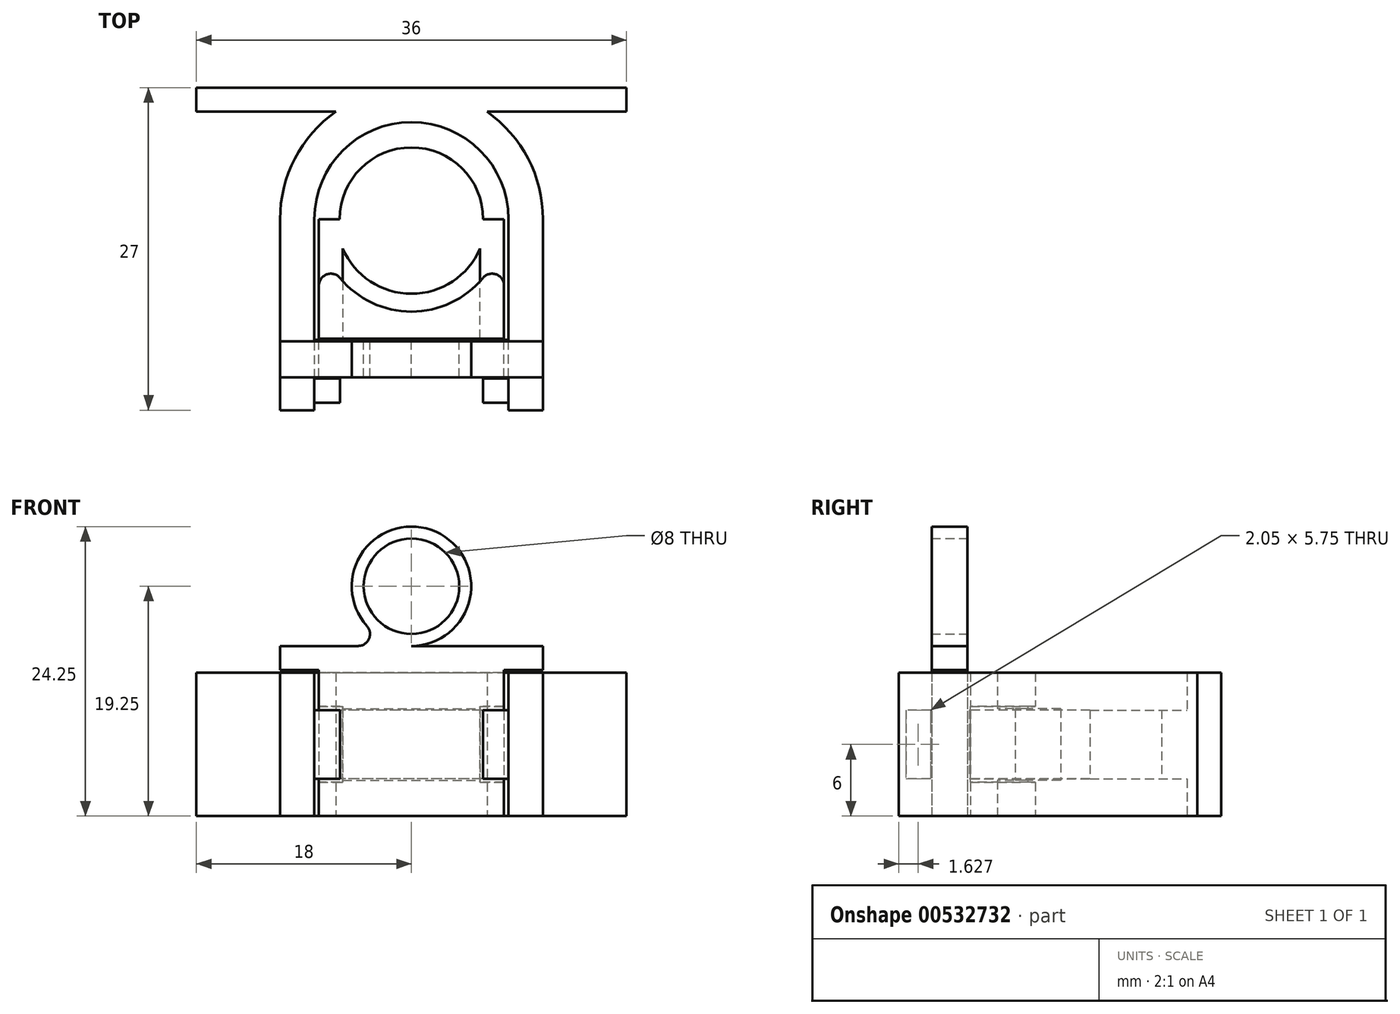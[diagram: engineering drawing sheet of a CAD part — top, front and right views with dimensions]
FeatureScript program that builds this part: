
annotation { "Feature Type Name" : "Feature", "Feature Type Description" : "" }
export const myFeature = defineFeature(function(context is Context, id is Id, definition is map)
    precondition{}
    {
        {
            var Q0;
            Q0=qCreatedBy(makeId("Top.planeOp"),FACE);
            var sketch = newSketch(context, id + "F0", { "sketchPlane" : qUnion([Q0])});
            skLineSegment(sketch, "E0", {"start": v(16.68, 0) * mm, "end": v(-18.88, 0) * mm, "construction": true});
            skLineSegment(sketch, "E1", {"start": v(-8.12, 0) * mm, "end": v(-8.12, -16) * mm});
            skLineSegment(sketch, "E2", {"start": v(-8.12, -16) * mm, "end": v(-11, -16) * mm});
            skLineSegment(sketch, "E3", {"start": v(-11, -16) * mm, "end": v(-11, 0) * mm});
            skLineSegment(sketch, "E4", {"start": v(11, 0) * mm, "end": v(11, -16) * mm});
            skLineSegment(sketch, "E5", {"start": v(11, -16) * mm, "end": v(8.12, -16) * mm});
            skLineSegment(sketch, "E6", {"start": v(8.12, -16) * mm, "end": v(8.12, 0) * mm});
            skArc(sketch, "E7", {"start": v(-8.12, 0) * mm, "mid": v(0, -8.12) * mm, "end": v(8.12, 0) * mm, "construction": true});
            skArc(sketch, "E8", {"start": v(8.12, 0) * mm, "mid": v(0, 8.12) * mm, "end": v(-8.12, 0) * mm});
            skArc(sketch, "E9", {"start": v(11, 0) * mm, "mid": v(0, 11) * mm, "end": v(-11, 0) * mm});
            skArc(sketch, "E10", {"start": v(-11, 0) * mm, "mid": v(0, -11) * mm, "end": v(11, 0) * mm, "construction": true});
            skArc(sketch, "E11", {"start": v(-5.99, -0.4) * mm, "mid": v(0, -6) * mm, "end": v(5.99, -0.4) * mm, "construction": true});
            skArc(sketch, "E12", {"start": v(5.99, -0.4) * mm, "mid": v(0, 6) * mm, "end": v(-5.99, -0.4) * mm});
            skLineSegment(sketch, "E13", {"start": v(0, 11) * mm, "end": v(-18, 11) * mm});
            skLineSegment(sketch, "E14", {"start": v(-18, 11) * mm, "end": v(-18, 9) * mm});
            skLineSegment(sketch, "E15", {"start": v(-18, 9) * mm, "end": v(-6.32, 9) * mm});
            skLineSegment(sketch, "E16", {"start": v(0, -19.46) * mm, "end": v(0, 22.13) * mm, "construction": true});
            skLineSegment(sketch, "E17.MirrorCS", {"start": v(0, 11) * mm, "end": v(18, 11) * mm});
            skLineSegment(sketch, "E18.MirrorCS", {"start": v(18, 9) * mm, "end": v(6.32, 9) * mm});
            skLineSegment(sketch, "E19.MirrorCS", {"start": v(18, 11) * mm, "end": v(18, 9) * mm});
            skLineSegment(sketch, "E20", {"start": v(-5.99, -0.4) * mm, "end": v(-5.99, -15.4) * mm});
            skLineSegment(sketch, "E21", {"start": v(-5.99, -15.4) * mm, "end": v(-8.12, -15.4) * mm});
            skLineSegment(sketch, "E22", {"start": v(5.99, -0.4) * mm, "end": v(5.99, -15.4) * mm});
            skLineSegment(sketch, "E23", {"start": v(5.99, -15.4) * mm, "end": v(8.12, -15.4) * mm});
            skLineSegment(sketch, "E24", {"start": v(-5.99, -10.1) * mm, "end": v(-8.12, -10.1) * mm});
            skLineSegment(sketch, "E25", {"start": v(-5.99, -13.35) * mm, "end": v(-8.12, -13.35) * mm});
            skLineSegment(sketch, "E26.MirrorCS", {"start": v(5.99, -10.1) * mm, "end": v(8.12, -10.1) * mm});
            skLineSegment(sketch, "E27.MirrorCS", {"start": v(5.99, -13.35) * mm, "end": v(8.12, -13.35) * mm});
            skSolve(sketch);
        }
        {
            var Q0;
            {var subQ0=sQuery(id+"F0.wireOp",EDGE,"E13");Q0=makeQuery(id+"F0.imprint","IMPRINT",FACE,{"disambiguationData":[TD([[makeQuery(id+"F0.imprint","IMPRINT",EDGE,{"derivedFrom":subQ0}),1.0]])]});}
            var Q1;
            {var subQ0=sQuery(id+"F0.wireOp",EDGE,"E17.MirrorCS");Q1=makeQuery(id+"F0.imprint","IMPRINT",FACE,{"disambiguationData":[TD([[makeQuery(id+"F0.imprint","IMPRINT",EDGE,{"derivedFrom":subQ0}),-1.0]])]});}
            var Q2;
            {var subQ9=sQuery(id+"F0.wireOp",EDGE,"E2");Q2=makeQuery(id+"F0.imprint","IMPRINT",FACE,{"disambiguationData":[TD([[makeQuery(id+"F0.imprint","IMPRINT",EDGE,{"derivedFrom":subQ9}),-1.0]])]});}
            extrude(context, id + "F1", {"entities" : qUnion([Q0, Q1, Q2]), "endBound" : BoundingType.SYMMETRIC, "depth" : 12 * mm, "offsetDistance" : 25 * mm});
        }
        {
            var Q0;
            {var subQ0=sQuery(id+"F0.wireOp",EDGE,"E8");Q0=makeQuery(id+"F0.imprint","IMPRINT",FACE,{"disambiguationData":[TD([[makeQuery(id+"F0.imprint","IMPRINT",EDGE,{"derivedFrom":subQ0}),1.0]])]});}
            var Q1;
            {var subQ0=sQuery(id+"F0.wireOp",EDGE,"E21");Q1=makeQuery(id+"F0.imprint","IMPRINT",FACE,{"disambiguationData":[TD([[makeQuery(id+"F0.imprint","IMPRINT",EDGE,{"derivedFrom":subQ0}),-1.0]])]});}
            var Q2;
            {var subQ0=sQuery(id+"F0.wireOp",EDGE,"E23");Q2=makeQuery(id+"F0.imprint","IMPRINT",FACE,{"disambiguationData":[TD([[makeQuery(id+"F0.imprint","IMPRINT",EDGE,{"derivedFrom":subQ0}),1.0]])]});}
            var Q3;
            Q3=sQuery(id+"F0.wireOp",EDGE,"E8");
            extrude(context, id + "F2", {"entities" : qUnion([Q0, Q1, Q2]), "operationType" : NewBodyOperationType.ADD, "surfaceEntities" : qUnion([Q3]), "endBound" : BoundingType.SYMMETRIC, "depth" : 5.75 * mm, "offsetDistance" : 25 * mm});
        }
        {
            var Q0;
            Q0=qCreatedBy(makeId("Top.planeOp"),FACE);
            var sketch = newSketch(context, id + "F3", { "sketchPlane" : qUnion([Q0])});
            skLineSegment(sketch, "E28", {"start": v(0, 21.73) * mm, "end": v(0, -21.78) * mm, "construction": true});
            skLineSegment(sketch, "E29", {"start": v(-21.07, 0) * mm, "end": v(6.25, 0) * mm, "construction": true});
            skLineSegment(sketch, "E30", {"start": v(-5.75, -2.45) * mm, "end": v(-5.75, -10) * mm});
            skLineSegment(sketch, "E31", {"start": v(5.75, -10) * mm, "end": v(5.75, -2.45) * mm});
            skLineSegment(sketch, "E32", {"start": v(-7.75, 0) * mm, "end": v(-7.75, -10) * mm});
            skLineSegment(sketch, "E33", {"start": v(-7.75, -10) * mm, "end": v(7.75, -10) * mm});
            skLineSegment(sketch, "E34", {"start": v(7.75, -10) * mm, "end": v(7.75, 0) * mm});
            skArc(sketch, "E35", {"start": v(-7.75, 0) * mm, "mid": v(0, -7.75) * mm, "end": v(7.75, 0) * mm});
            skArc(sketch, "E36", {"start": v(7.75, 0) * mm, "mid": v(0, 7.75) * mm, "end": v(-7.75, 0) * mm, "construction": true});
            skLineSegment(sketch, "E37", {"start": v(6.25, 0) * mm, "end": v(23.4, 0) * mm, "construction": true});
            skArc(sketch, "E38", {"start": v(-5.75, -2.45) * mm, "mid": v(0, -6.25) * mm, "end": v(5.75, -2.45) * mm});
            skArc(sketch, "E39", {"start": v(5.75, -2.45) * mm, "mid": v(0, 6.25) * mm, "end": v(-5.75, -2.45) * mm, "construction": true});
            skLineSegment(sketch, "E40", {"start": v(5.75, -2.45) * mm, "end": v(5.75, 0) * mm});
            skLineSegment(sketch, "E41", {"start": v(5.75, 0) * mm, "end": v(7.75, 0) * mm});
            skLineSegment(sketch, "E42", {"start": v(-5.75, -2.45) * mm, "end": v(-5.75, 0) * mm});
            skLineSegment(sketch, "E43", {"start": v(-5.75, 0) * mm, "end": v(-7.75, 0) * mm});
            skSolve(sketch);
        }
        {
            var Q0;
            {var subQ5=sQuery(id+"F3.wireOp",EDGE,"E32");Q0=makeQuery(id+"F3.imprint","IMPRINT",FACE,{"disambiguationData":[TD([[makeQuery(id+"F3.imprint","IMPRINT",EDGE,{"derivedFrom":subQ5}),1.0]])]});}
            var Q1;
            {var subQ1=sQuery(id+"F3.wireOp",EDGE,"wfdL85CV-VBdl-9YlV-2M5o-2CQI3bBZQMcm");var subQ5=sQuery(id+"F3.wireOp",EDGE,"E30");var subQ6=makeQuery(id+"F3.imprint","INTERSECT",VERTEX,{"derivedFrom":[subQ1,subQ5]});Q1=makeQuery(id+"F3.imprint","IMPRINT",FACE,{"disambiguationData":[TD([[makeQuery(id+"F3.imprint","IMPRINT",EDGE,{"disambiguationData":[TD([[subQ6,1.0]])],"derivedFrom":subQ1}),-1.0]])]});}
            var Q2;
            {var subQ0=sQuery(id+"F3.wireOp",EDGE,"E30");var subQ1=sQuery(id+"F3.wireOp",EDGE,"wfdL85CV-VBdl-9YlV-2M5o-2CQI3bBZQMcm");var subQ2=makeQuery(id+"F3.imprint","INTERSECT",VERTEX,{"derivedFrom":[subQ1,subQ0]});Q2=makeQuery(id+"F3.imprint","IMPRINT",FACE,{"disambiguationData":[TD([[makeQuery(id+"F3.imprint","IMPRINT",EDGE,{"disambiguationData":[TD([[subQ2,-1.0]])],"derivedFrom":subQ1}),-1.0]])]});}
            var Q3;
            {var subQ0=sQuery(id+"F3.wireOp",EDGE,"E33");var subQ1=sQuery(id+"F3.wireOp",EDGE,"E30");var subQ2=makeQuery(id+"F3.imprint","INTERSECT",VERTEX,{"derivedFrom":[subQ1,subQ0]});Q3=makeQuery(id+"F3.imprint","IMPRINT",FACE,{"disambiguationData":[TD([[makeQuery(id+"F3.imprint","IMPRINT",EDGE,{"disambiguationData":[TD([[subQ2,1.0]])],"derivedFrom":subQ1}),1.0]])]});}
            var Q4;
            {var subQ5=sQuery(id+"F3.wireOp",EDGE,"E34");Q4=makeQuery(id+"F3.imprint","IMPRINT",FACE,{"disambiguationData":[TD([[makeQuery(id+"F3.imprint","IMPRINT",EDGE,{"derivedFrom":subQ5}),1.0]])]});}
            var Q5;
            {var subQ0=sQuery(id+"F3.wireOp",EDGE,"wfdL85CV-VBdl-9YlV-2M5o-2CQI3bBZQMcm");var subQ1=makeQuery(id+"F3.imprint","INTERSECT",VERTEX,{"derivedFrom":[subQ0,sQuery(id+"F3.wireOp",EDGE,"E30")]});Q5=makeQuery(id+"F3.imprint","IMPRINT",FACE,{"disambiguationData":[TD([[makeQuery(id+"F3.imprint","IMPRINT",EDGE,{"disambiguationData":[TD([[subQ1,-1.0]])],"derivedFrom":subQ0}),1.0]])]});}
            extrude(context, id + "F4", {"entities" : qUnion([Q0, Q1, Q2, Q3, Q4, Q5]), "endBound" : BoundingType.SYMMETRIC, "depth" : 12 * mm, "offsetDistance" : 25 * mm});
        }
        {
            var Q0;
            {var subQ0=sQuery(id+"F3.wireOp",EDGE,"E38");Q0=makeQuery(id+"F3.imprint","IMPRINT",FACE,{"disambiguationData":[TD([[makeQuery(id+"F3.imprint","IMPRINT",EDGE,{"derivedFrom":subQ0}),-1.0]])]});}
            extrude(context, id + "F5", {"entities" : qUnion([Q0]), "operationType" : NewBodyOperationType.ADD, "endBound" : BoundingType.SYMMETRIC, "depth" : 6 * mm, "offsetDistance" : 25 * mm});
        }
        {
            var Q0;
            {var subQ0=sQuery(id+"F3.wireOp",EDGE,"E40");Q0=makeQuery(id+"F3.imprint","IMPRINT",FACE,{"disambiguationData":[TD([[makeQuery(id+"F3.imprint","IMPRINT",EDGE,{"derivedFrom":subQ0}),-1.0]])]});}
            var Q1;
            {var subQ5=sQuery(id+"F3.wireOp",EDGE,"E34");Q1=makeQuery(id+"F3.imprint","IMPRINT",FACE,{"disambiguationData":[TD([[makeQuery(id+"F3.imprint","IMPRINT",EDGE,{"derivedFrom":subQ5}),1.0]])]});}
            var Q2;
            {var subQ0=sQuery(id+"F3.wireOp",EDGE,"E42");Q2=makeQuery(id+"F3.imprint","IMPRINT",FACE,{"disambiguationData":[TD([[makeQuery(id+"F3.imprint","IMPRINT",EDGE,{"derivedFrom":subQ0}),1.0]])]});}
            var Q3;
            {var subQ5=sQuery(id+"F3.wireOp",EDGE,"E32");Q3=makeQuery(id+"F3.imprint","IMPRINT",FACE,{"disambiguationData":[TD([[makeQuery(id+"F3.imprint","IMPRINT",EDGE,{"derivedFrom":subQ5}),1.0]])]});}
            extrude(context, id + "F6", {"entities" : qUnion([Q0, Q1, Q2, Q3]), "operationType" : NewBodyOperationType.REMOVE, "endBound" : BoundingType.SYMMETRIC, "oppositeDirection" : true, "depth" : 6.35 * mm, "offsetDistance" : 25 * mm});
        }
        {
            var Q0;
            Q0=qCreatedBy(makeId("Front.planeOp"),FACE);
            cPlane(context, id + "F7", {"entities" : qUnion([Q0]), "cplaneType" : CPlaneType.OFFSET, "offset" : 10.25 * mm, "width" : 150 * mm, "height" : 150 * mm});
        }
        {
            var Q0;
            Q0=qCreatedBy(id+"F7.planeOp",FACE);
            var sketch = newSketch(context, id + "F8", { "sketchPlane" : qUnion([Q0])});
            skLineSegment(sketch, "E44", {"start": v(0, 15.78) * mm, "end": v(0, -19.04) * mm, "construction": true});
            skLineSegment(sketch, "E45", {"start": v(32.6, 0) * mm, "end": v(-26.62, 0) * mm, "construction": true});
            skLineSegment(sketch, "E46", {"start": v(0, 8.25) * mm, "end": v(-11, 8.25) * mm});
            skLineSegment(sketch, "E47", {"start": v(-11, 8.25) * mm, "end": v(-11, 6.25) * mm});
            skLineSegment(sketch, "E48", {"start": v(-11, 6.25) * mm, "end": v(-7.75, 6.25) * mm});
            skLineSegment(sketch, "E49", {"start": v(-7.75, 6.25) * mm, "end": v(-7.75, -6) * mm});
            skLineSegment(sketch, "E50", {"start": v(-7.75, -6) * mm, "end": v(0, -6) * mm});
            skLineSegment(sketch, "E51.MirrorCS", {"start": v(0, 8.25) * mm, "end": v(11, 8.25) * mm});
            skLineSegment(sketch, "E52.MirrorCS", {"start": v(11, 8.25) * mm, "end": v(11, 6.25) * mm});
            skLineSegment(sketch, "E53.MirrorCS", {"start": v(11, 6.25) * mm, "end": v(7.75, 6.25) * mm});
            skLineSegment(sketch, "E54.MirrorCS", {"start": v(7.75, 6.25) * mm, "end": v(7.75, -6) * mm});
            skLineSegment(sketch, "E55.MirrorCS", {"start": v(7.75, -6) * mm, "end": v(0, -6) * mm});
            skCircle(sketch, "E56", {"center": v(0, 13.25) * mm, "radius": 5 * mm});
            skCircle(sketch, "E57", {"center": v(0, 13.25) * mm, "radius": 4 * mm});
            skArc(sketch, "E58", {"start": v(-3.73, 9.92) * mm, "mid": v(-5.39, 9.66) * mm, "end": v(-4.47, 8.25) * mm, "construction": true});
            skArc(sketch, "E59", {"start": v(-4.47, 8.25) * mm, "mid": v(-3.56, 8.84) * mm, "end": v(-3.73, 9.92) * mm});
            skArc(sketch, "E60.MirrorCS", {"start": v(4.47, 8.25) * mm, "mid": v(3.56, 8.84) * mm, "end": v(3.73, 9.92) * mm});
            skSolve(sketch);
        }
        {
            var Q0;
            Q0=makeQuery(id+"F8.imprint","IMPRINT",FACE,{"disambiguationData":[TD([[makeQuery(id+"F8.imprint","IMPRINT",EDGE,{"derivedFrom":sQuery(id+"F8.wireOp",EDGE,"E56")}),1.0]])]});
            var Q1;
            Q1=makeQuery(id+"F8.imprint","IMPRINT",FACE,{"disambiguationData":[TD([[makeQuery(id+"F8.imprint","IMPRINT",EDGE,{"derivedFrom":sQuery(id+"F8.wireOp",EDGE,"E46")}),1.0]])]});
            var Q2;
            {var subQ3=sQuery(id+"F8.wireOp",EDGE,"E59");Q2=makeQuery(id+"F8.imprint","IMPRINT",FACE,{"disambiguationData":[TD([[makeQuery(id+"F8.imprint","IMPRINT",EDGE,{"derivedFrom":subQ3}),-1.0]])]});}
            var Q3;
            {var subQ3=sQuery(id+"F8.wireOp",EDGE,"E60.MirrorCS");Q3=makeQuery(id+"F8.imprint","IMPRINT",FACE,{"disambiguationData":[TD([[makeQuery(id+"F8.imprint","IMPRINT",EDGE,{"derivedFrom":subQ3}),1.0]])]});}
            extrude(context, id + "F9", {"entities" : qUnion([Q0, Q1, Q2, Q3]), "depth" : 3 * mm, "offsetDistance" : 25 * mm});
        }
        {
            var Q0;
            {var subQ0=sQuery(id+"F3.wireOp",EDGE,"E32");var subQ1=sQuery(id+"F3.wireOp",EDGE,"E35");var subQ2=sQuery(id+"F3.wireOp",EDGE,"E33");var subQ3=sQuery(id+"F3.wireOp",EDGE,"E43");Q0=makeQuery(id+"F6.boolean.opBoolean","SPLIT",EDGE,{"disambiguationData":[TD([makeQuery(id+"F4.opExtrude","CAP_FACE",FACE,{"disambiguationData":[OSD([subQ0,subQ2,sQuery(id+"F3.wireOp",EDGE,"E34"),subQ1])],"isStart":false})])],"derivedFrom":makeQuery(id+"F4.opExtrude","SWEPT_EDGE",EDGE,{"disambiguationData":[OSD([subQ0,subQ1,subQ3])]})});}
            var Q1;
            {var subQ0=sQuery(id+"F3.wireOp",EDGE,"E32");var subQ1=sQuery(id+"F3.wireOp",EDGE,"E35");var subQ2=sQuery(id+"F3.wireOp",EDGE,"E33");var subQ3=sQuery(id+"F3.wireOp",EDGE,"E43");Q1=makeQuery(id+"F6.boolean.opBoolean","SPLIT",EDGE,{"disambiguationData":[TD([makeQuery(id+"F4.opExtrude","CAP_FACE",FACE,{"disambiguationData":[OSD([subQ0,subQ2,sQuery(id+"F3.wireOp",EDGE,"E34"),subQ1])],"isStart":true})])],"derivedFrom":makeQuery(id+"F4.opExtrude","SWEPT_EDGE",EDGE,{"disambiguationData":[OSD([subQ0,subQ1,subQ3])]})});}
            var Q2;
            {var subQ0=sQuery(id+"F3.wireOp",EDGE,"E35");var subQ1=sQuery(id+"F3.wireOp",EDGE,"E34");var subQ2=sQuery(id+"F3.wireOp",EDGE,"E33");var subQ3=sQuery(id+"F3.wireOp",EDGE,"E41");Q2=makeQuery(id+"F6.boolean.opBoolean","SPLIT",EDGE,{"disambiguationData":[TD([makeQuery(id+"F4.opExtrude","CAP_FACE",FACE,{"disambiguationData":[OSD([sQuery(id+"F3.wireOp",EDGE,"E32"),subQ2,subQ1,subQ0])],"isStart":true})])],"derivedFrom":makeQuery(id+"F4.opExtrude","SWEPT_EDGE",EDGE,{"disambiguationData":[OSD([subQ1,subQ0,subQ3])]})});}
            var Q3;
            {var subQ0=sQuery(id+"F3.wireOp",EDGE,"E35");var subQ1=sQuery(id+"F3.wireOp",EDGE,"E34");var subQ2=sQuery(id+"F3.wireOp",EDGE,"E33");var subQ3=sQuery(id+"F3.wireOp",EDGE,"E41");Q3=makeQuery(id+"F6.boolean.opBoolean","SPLIT",EDGE,{"disambiguationData":[TD([makeQuery(id+"F4.opExtrude","CAP_FACE",FACE,{"disambiguationData":[OSD([sQuery(id+"F3.wireOp",EDGE,"E32"),subQ2,subQ1,subQ0])],"isStart":false})])],"derivedFrom":makeQuery(id+"F4.opExtrude","SWEPT_EDGE",EDGE,{"disambiguationData":[OSD([subQ1,subQ0,subQ3])]})});}
            fillet(context, id + "F10", {"entities" : qUnion([Q0, Q1, Q2, Q3]), "radius" : 1 * mm, "tangentPropagation" : true, "allowEdgeOverflow" : false});
        }
    });
